# Revit family: TEMID_Металлодетектор_арочный_ZK-D1065 (1000мм)_980мм
name_source: partatom
category: Охранная сигнализация
units: mm (PartAtom-declared; Revit-internal decimal feet)

## family parameters
Всегда вертикально = Нет
На основе рабочей плоскости = Нет
Общий = Да
При загрузке вырезать с полостями = Нет
Размер круглого соединителя = Использовать диаметр
Сохранять ориентацию аннотаций = Нет
Тип детали = Нормальный
Точка расчета площади = Да

## types (1)
- ZK-D1065 (1000 мм)_Проход 980 мм
    =Габариты= = =Габариты=
    ADSK_Единица измерения = шт.
    ADSK_Завод-изготовитель = TEMID
    ADSK_Количество = 1
    ADSK_Марка = ZK-D1065 (1000 мм)
    ADSK_Наименование = Арочный металлодетектор, ширина прохода 980±10 мм, 6 зон детектирования, 100 уровней чувст-ти, 3.5  ЖК дисплей, подсчет количества людей и срабатываний тревоги, материал огнестойкий и влагостойкий ПВХ, -20°C - 55°C
    ADSK_Обозначение = RD
    ADSK_Раздел спецификации = 3. Периферийное оборудование
    ADSK_Размер_Высота = 2218 мм
    ADSK_Размер_Глубина = 520 мм
    ADSK_Размер_Ширина = 980 мм
    ADSK_Тип = ZK-D1065 (1000 мм)
    URL = https://temid-global.ru
    Высота передних панелей = 300 мм
    Глубина боковых панелей = 420 мм
    Глубина между панелями = 270 мм
    Зона обслуживания_Отступ от прибора = 150 мм
    Материал = Серый
    Материал болтов = Белый
    Материал зоны = Зона металлоискателя
    Материал экран = Бледно-жёлтый
    Отметка по умолчанию = 0 мм
    Текст_модели = ZK-D1065 (1000 мм)
    Экран_Высота = 150 мм
    Экран_Отступ = 0 мм
    Экран_Угол наклон = 90.00°
    Экран_Ширина = 100 мм
